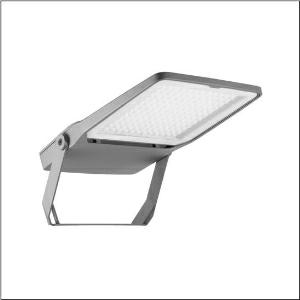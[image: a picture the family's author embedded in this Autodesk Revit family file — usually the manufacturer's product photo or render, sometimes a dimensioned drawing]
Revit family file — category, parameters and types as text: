
# Revit family: floodlight_fl_20_midi___rs17_5xa7682e1b1ac_fe9e
name_source: partatom
category: Lighting Fixtures
units: mm (PartAtom-declared; Revit-internal decimal feet)

## family parameters
Cut with Voids When Loaded = No
Host = Face
Light Source = No
Part Type = Normal
Room Calculation Point = No
Round Connector Dimension = Use Diameter
Shared = No

## types (1)
- --- (1 x LED 3000K / CRI = 80 (unbekannt), 22840 lm, 3000K)
    Apparent Load = 208 VA
    CIE Flux Codes = 79 92 99 100 100
    Color Rendering = 80
    Color Temperature = 3000K
    Default Elevation = 1800 mm
    Description = Floodlight FL 20 midi, floodlight, primary light control with lens, of plastic, primary optical cover: protective disc, of toughened safety glass, transparent, light distribution: RS17, light emission: direct distribution, primary light characteristic: rotationally symmetric, installation type: surface-mounted, LED, High Power LED, rated luminous flux: 22.840lm, luminous efficacy: 110lm/W, light colour: 830, colour temperature: 3000K, control gear: ECG Plus, control: flexible luminous flux parameterisation, time-dependent luminous flux control, digital communication interface, power reduction, overheat protection, electronic power reduction, with terminal, 5-pole, max. 2.5mm², mains connection: 220..240V, AC, 50/60Hz, rated input power: 208W, LED unit, of diecast aluminium, powder-coated, Siteco® metallic grey (DB 702S), corrosivity category C5 mid according to DIN EN ISO 12944, incl. 1x M20 cable gland for cable Ø 6.5..12mm, length: 654mm, width: 450mm, height: 76mm, housing frame, of diecast aluminium, powder-coated, Siteco® metallic grey (DB 702S), mounting bracket, of steel, powder-coated, Siteco® metallic grey (DB 702S), DALI, protection rating (complete): IP66, insulation class (complete): insulation class II (safety insulation), certification: CE, ENEC, VDE, protection symbol: D, permissible operating ambient temperature: -40..+40°C, permissible operating ambient temperature for outdoor applications: -40..+50°C, standard: DIN EN 12944, packaging unit: 1 piece

Light Distribution: RS17
    Height = 76 mm
    Lamp = 1 x LED 3000K / CRI >= 80 (unbekannt)
    Lamp Light Flux = 22840 lm
    Lamp count = 1
    Length = 672 mm
    Luminous efficacy = 110 lm/W
    Manufacturer = Siteco
    ModVariant = No
    Model = 5XA7682E1B1AC
    Mounting Place = Wall
    Mounting Type = Surface mounted
    Number of Poles = 1
    OnlyDefault = Yes
    Power Factor = 1
    Product Name = Floodlight FL 20 midi | RS17
    Product group = floodlight | wall mounted
    ProductGroupID = 2001
    Protection Class = Protection class II
    Protection Degree = IP 66
    RLX_Detail_Level = 1
    RLX_Emergency_Light_Flux = 0 lm
    RLX_Emergency_Type = 0
    RLX_Emergency_Type_DB = No
    RlxData = <blob elided: 92281 chars, md5=c74363d6>
    Socket = socket
    Standby Power = 0 W
    System Light Flux = 22840 lm
    System Power = 208 W
    Type Comments = factory setting: luminous flux: 100 % | dim-lin: 254 | 484 mA
    Type Image = l_1005943.jpg
    URL = http://relux.com
    VarID = @adj_146521
    Voltage = 0 V
    Weight = 0.00 kg
    Width = 450 mm

## geometry (parser evidence)
native form markers: Blend x4, Sweep x14
no freeform markers — native parametric forms only
